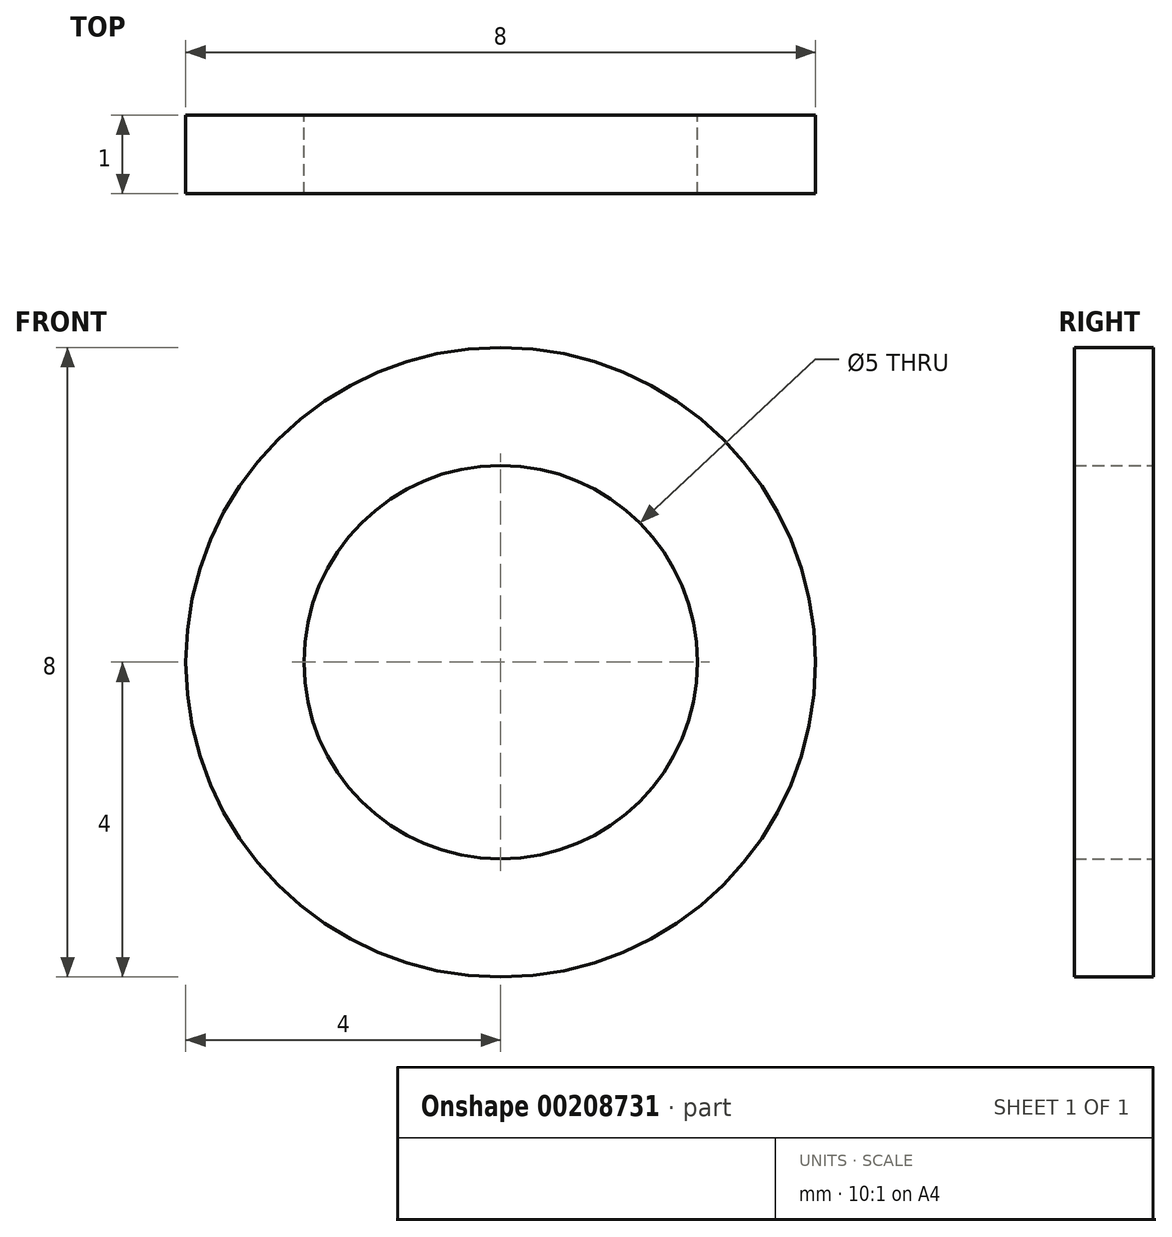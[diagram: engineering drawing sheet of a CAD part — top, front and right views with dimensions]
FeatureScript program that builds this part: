
annotation { "Feature Type Name" : "Feature", "Feature Type Description" : "" }
export const myFeature = defineFeature(function(context is Context, id is Id, definition is map)
    precondition{}
    {
        {
            var Q0;
            Q0=qCreatedBy(makeId("Front.planeOp"),FACE);
            var sketch = newSketch(context, id + "F0", { "sketchPlane" : qUnion([Q0])});
            skCircle(sketch, "E0", {"center": v(0, 0) * mm, "radius": 4 * mm});
            skCircle(sketch, "E1", {"center": v(0, 0) * mm, "radius": 2.5 * mm});
            skSolve(sketch);
        }
        {
            var Q0;
            Q0=qSketchRegion(id+"F0",true);
            extrude(context, id + "F1", {"entities" : qUnion([Q0]), "depth" : 1 * mm});
        }
    });
